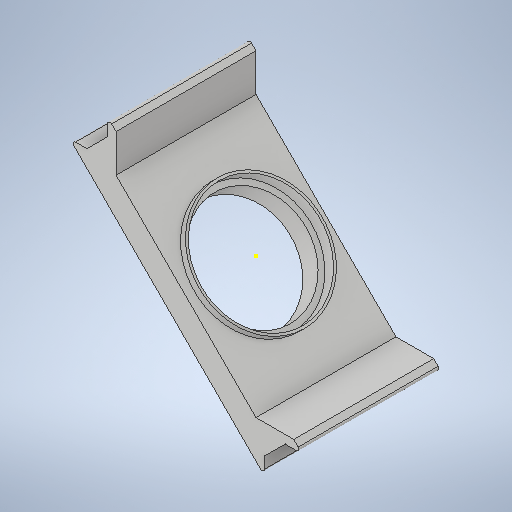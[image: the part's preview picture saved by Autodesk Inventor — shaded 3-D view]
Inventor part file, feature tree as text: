
AUTODESK INVENTOR PART (.ipt)
format: ipt  version: 2025.1 (Build 291241000, 241)  size: 307,200 bytes
history: native  units: mm
features: sketch x6, fillet x4, extrude x2, hole x2
ambient origin geometry x8: Origin, YZ Plane, XZ Plane, XY Plane, X Axis, Y Axis, Z Axis, Center Point
bodies: 实体1 (feature_tree)
feature tree (14):
  extrude  "拉伸1"  Depth=0.5mm
  hole  "孔1"  [1 undecoded]
  sketch  "草图3"  dims[d18=0.5mm d19=25.4mm]
  sketch  "草图4"  dims[d20=1.5mm d21=0.0mm]
  extrude  "拉伸2"  Depth=0.5mm
  hole  "孔2"  [1 undecoded]
  fillet  "圆角1"  Radius=0.5mm
  fillet  "圆角2"  [1 undecoded]
  fillet  "圆角3"  [1 undecoded]
  fillet  "圆角4"  [1 undecoded]
  sketch  "草图1"  dims[d6=15.0mm d7=15.0mm d8=0.0mm d9=0.0mm]
  sketch  "草图2"  dims[d10=23.0mm d11=6.0mm d12=25.4mm d13=1.1mm d14=90.0deg d15=0.5mm d16=20.594885mm]
  sketch  "草图5"  dims[d22=25.4mm d23=6.0mm d24=4.0mm d25=2.0mm d26=90.0deg d27=8.0mm d28=20.594885mm d29=0.5mm]
  sketch  "草图6"  dims[d30=0.5mm d31=0.5mm d32=0.5mm d33=0.0mm]
note: 5 required parameter values undecoded (feature->parameter linkage not recoverable at this tier; creation-order binding heuristic only, values carry confidence <= 0.55)
